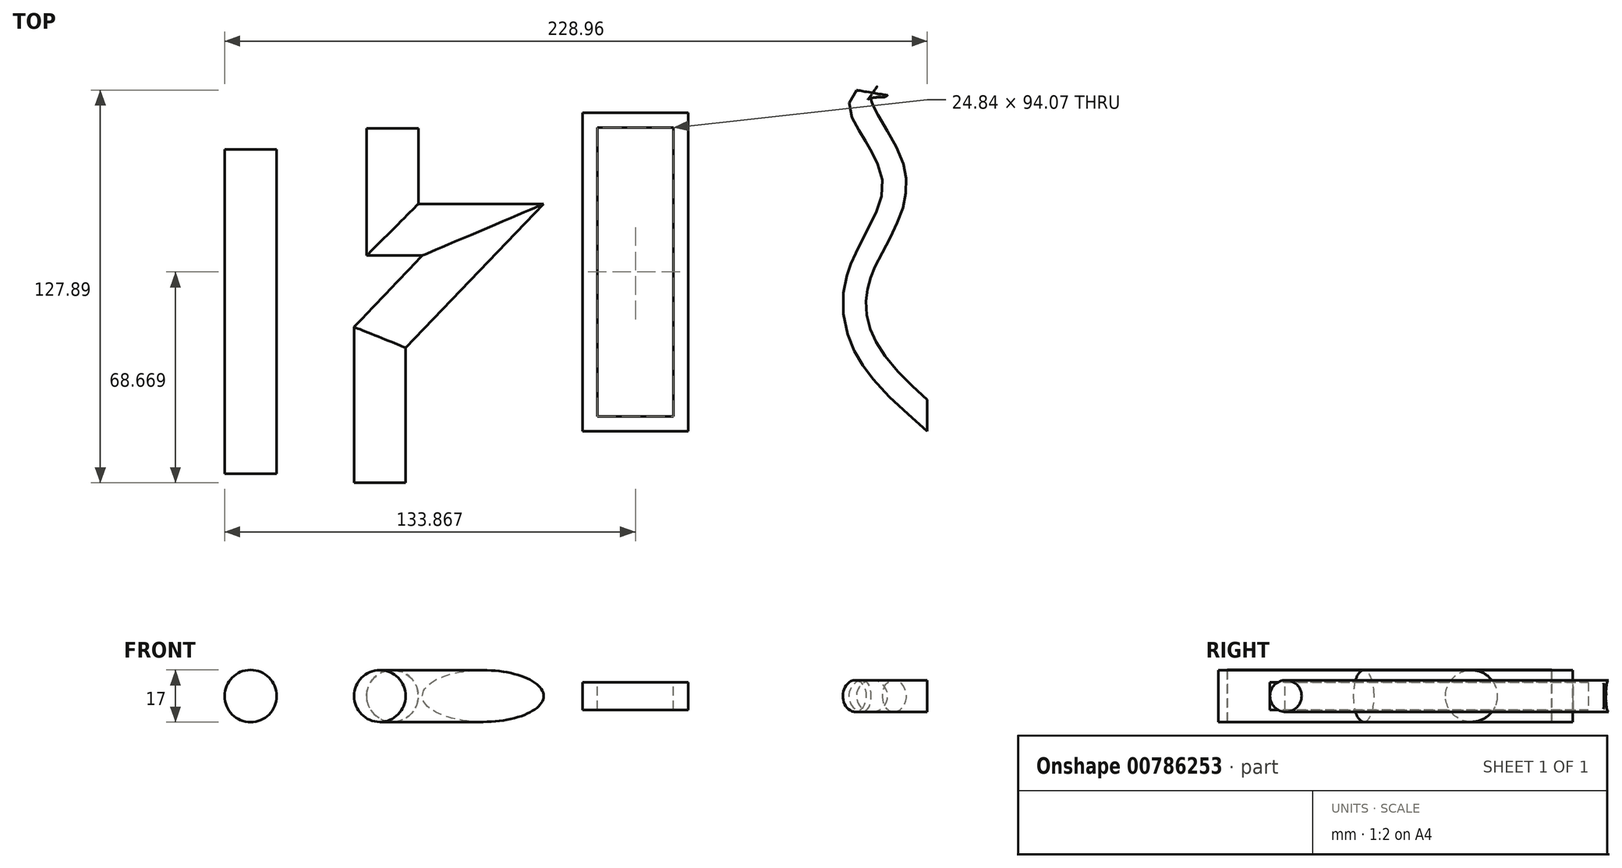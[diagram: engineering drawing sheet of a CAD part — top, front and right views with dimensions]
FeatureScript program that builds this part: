
annotation { "Feature Type Name" : "Feature", "Feature Type Description" : "" }
export const myFeature = defineFeature(function(context is Context, id is Id, definition is map)
    precondition{}
    {
        {
            var Q0;
            Q0=qCreatedBy(makeId("Top.planeOp"),FACE);
            var sketch = newSketch(context, id + "F0", { "sketchPlane" : qUnion([Q0])});
            skLineSegment(sketch, "E0", {"start": v(-111.04, -65.23) * mm, "end": v(-111.04, 40.34) * mm});
            skLineSegment(sketch, "E1", {"start": v(-111.04, 40.34) * mm, "end": v(-113.85, 40.34) * mm});
            skLineSegment(sketch, "E2", {"start": v(-69.94, -68.18) * mm, "end": v(-69.94, -20.22) * mm});
            skLineSegment(sketch, "E3", {"start": v(-69.94, -20.22) * mm, "end": v(-38.4, 12.7) * mm});
            skLineSegment(sketch, "E4", {"start": v(-38.4, 12.7) * mm, "end": v(-65.84, 12.7) * mm});
            skLineSegment(sketch, "E5", {"start": v(-65.84, 12.7) * mm, "end": v(-65.84, 47.23) * mm});
            skLineSegment(sketch, "E6.bottom", {"start": v(0, -48.96) * mm, "end": v(29.67, -48.96) * mm});
            skLineSegment(sketch, "E6.top", {"start": v(0, 49.94) * mm, "end": v(29.67, 49.94) * mm});
            skLineSegment(sketch, "E6.left", {"start": v(0, -48.96) * mm, "end": v(0, 49.94) * mm});
            skLineSegment(sketch, "E6.right", {"start": v(29.67, -48.96) * mm, "end": v(29.67, 49.94) * mm});
            skFitSpline(sketch, "E7", {"points": [v(109.93, -47.05) * mm, v(89.59, -24.7) * mm, v(87.45, 0) * mm, v(98.26, 30.57) * mm, v(88.2, 54.14) * mm, v(91.12, 59) * mm], "startDerivative": vector(-102.7, 90.72) * mm, "endDerivative": vector(46.83, 38.22) * mm});
            skSolve(sketch);
        }
        {
            var Q0;
            Q0=sQuery(id+"F0.wireOp",VERTEX,"E0.start");
            var Q1;
            Q1=qCreatedBy(makeId("Front.planeOp"),FACE);
            cPlane(context, id + "F1", {"entities" : qUnion([Q0, Q1]), "cplaneType" : CPlaneType.PLANE_POINT, "offset" : 25 * mm, "width" : 150 * mm, "height" : 150 * mm});
        }
        {
            var Q0;
            Q0=sQuery(id+"F0.wireOp",VERTEX,"E2.start");
            var Q1;
            Q1=qCreatedBy(makeId("Front.planeOp"),FACE);
            cPlane(context, id + "F2", {"entities" : qUnion([Q0, Q1]), "cplaneType" : CPlaneType.PLANE_POINT, "offset" : 25 * mm, "width" : 150 * mm, "height" : 150 * mm});
        }
        {
            var Q0;
            Q0=sQuery(id+"F0.wireOp",VERTEX,"E6.bottom.start");
            var Q1;
            Q1=qCreatedBy(makeId("Front.planeOp"),FACE);
            cPlane(context, id + "F3", {"entities" : qUnion([Q0, Q1]), "cplaneType" : CPlaneType.PLANE_POINT, "offset" : 25 * mm, "width" : 150 * mm, "height" : 150 * mm});
        }
        {
            var Q0;
            Q0=qCreatedBy(id+"F1.planeOp",FACE);
            var sketch = newSketch(context, id + "F4", { "sketchPlane" : qUnion([Q0])});
            skCircle(sketch, "E8", {"center": v(-110.54, 0) * mm, "radius": 8.5 * mm});
            skSolve(sketch);
        }
        {
            var Q0;
            Q0=qCreatedBy(id+"F2.planeOp",FACE);
            var sketch = newSketch(context, id + "F5", { "sketchPlane" : qUnion([Q0])});
            skCircle(sketch, "E9", {"center": v(-68.41, 0) * mm, "radius": 8.43 * mm});
            skSolve(sketch);
        }
        {
            var Q0;
            Q0=qCreatedBy(id+"F3.planeOp",FACE);
            var sketch = newSketch(context, id + "F6", { "sketchPlane" : qUnion([Q0])});
            skLineSegment(sketch, "E10.bottom", {"start": v(2.42, -4.49) * mm, "end": v(-2.42, -4.49) * mm});
            skLineSegment(sketch, "E10.top", {"start": v(2.42, 4.49) * mm, "end": v(-2.42, 4.49) * mm});
            skLineSegment(sketch, "E10.left", {"start": v(2.42, -4.49) * mm, "end": v(2.42, 4.49) * mm});
            skLineSegment(sketch, "E10.right", {"start": v(-2.42, -4.49) * mm, "end": v(-2.42, 4.49) * mm});
            skPoint(sketch, "E10.middle", {"position": v(0, 0) * mm});
            skSolve(sketch);
        }
        {
            var Q0;
            Q0=makeQuery(id+"F4.imprint","IMPRINT",FACE,{"disambiguationData":[TD([[makeQuery(id+"F4.imprint","IMPRINT",EDGE,{"derivedFrom":sQuery(id+"F4.wireOp",EDGE,"E8")}),1.0]])]});
            var Q1;
            Q1=sQuery(id+"F0.wireOp",EDGE,"E0");
            sweep(context, id + "F7", {"profiles" : qUnion([Q0]), "path" : qUnion([Q1])});
        }
        {
            var Q0;
            Q0=makeQuery(id+"F5.imprint","IMPRINT",FACE,{"disambiguationData":[TD([[makeQuery(id+"F5.imprint","IMPRINT",EDGE,{"derivedFrom":sQuery(id+"F5.wireOp",EDGE,"E9")}),1.0]])]});
            var Q1;
            Q1=sQuery(id+"F0.wireOp",EDGE,"E3");
            var Q2;
            Q2=sQuery(id+"F0.wireOp",EDGE,"E2");
            var Q3;
            Q3=sQuery(id+"F0.wireOp",EDGE,"E5");
            var Q4;
            Q4=sQuery(id+"F0.wireOp",EDGE,"E4");
            sweep(context, id + "F8", {"profiles" : qUnion([Q0]), "path" : qUnion([Q1, Q2, Q3, Q4])});
        }
        {
            var Q0;
            Q0=makeQuery(id+"F6.imprint","IMPRINT",FACE,{"disambiguationData":[TD([[makeQuery(id+"F6.imprint","IMPRINT",EDGE,{"derivedFrom":sQuery(id+"F6.wireOp",EDGE,"E10.bottom")}),-1.0]])]});
            var Q1;
            Q1=sQuery(id+"F0.wireOp",EDGE,"E6.right");
            var Q2;
            Q2=sQuery(id+"F0.wireOp",EDGE,"E6.left");
            var Q3;
            Q3=sQuery(id+"F0.wireOp",EDGE,"E6.top");
            var Q4;
            Q4=sQuery(id+"F0.wireOp",EDGE,"E6.bottom");
            sweep(context, id + "F9", {"profiles" : qUnion([Q0]), "path" : qUnion([Q1, Q2, Q3, Q4])});
        }
        {
            var Q0;
            Q0=qCreatedBy(makeId("Right.planeOp"),FACE);
            var Q1;
            Q1=sQuery(id+"F0.wireOp",VERTEX,"E7.start");
            cPlane(context, id + "F10", {"entities" : qUnion([Q0, Q1]), "cplaneType" : CPlaneType.PLANE_POINT, "offset" : 25 * mm, "width" : 150 * mm, "height" : 150 * mm});
        }
        {
            var Q0;
            Q0=qCreatedBy(id+"F10.planeOp",FACE);
            var sketch = newSketch(context, id + "F11", { "sketchPlane" : qUnion([Q0])});
            skCircle(sketch, "E11", {"center": v(-46.23, 0) * mm, "radius": 5.15 * mm});
            skSolve(sketch);
        }
        {
            var Q0;
            Q0=makeQuery(id+"F11.imprint","IMPRINT",FACE,{"disambiguationData":[TD([[makeQuery(id+"F11.imprint","IMPRINT",EDGE,{"derivedFrom":sQuery(id+"F11.wireOp",EDGE,"E11")}),1.0]])]});
            var Q1;
            Q1=sQuery(id+"F0.wireOp",EDGE,"E7");
            sweep(context, id + "F12", {"profiles" : qUnion([Q0]), "path" : qUnion([Q1])});
        }
    });
